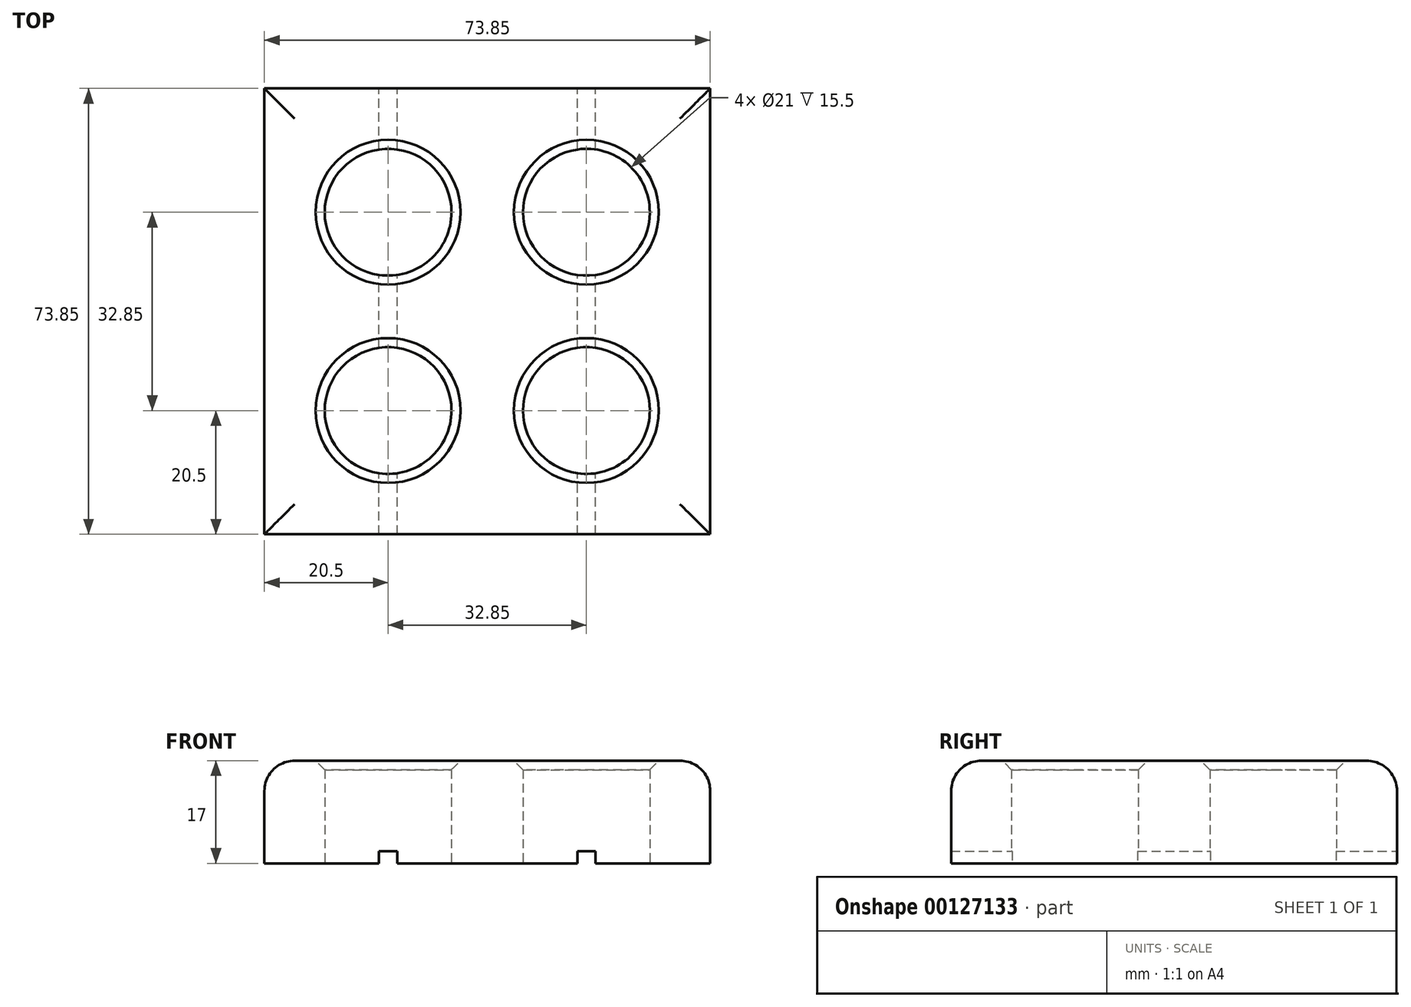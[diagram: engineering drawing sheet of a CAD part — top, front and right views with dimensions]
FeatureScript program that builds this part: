
annotation { "Feature Type Name" : "Feature", "Feature Type Description" : "" }
export const myFeature = defineFeature(function(context is Context, id is Id, definition is map)
    precondition{}
    {
        {
            var Q0;
            Q0=qCreatedBy(makeId("Top.planeOp"),FACE);
            var sketch = newSketch(context, id + "F0", { "sketchPlane" : qUnion([Q0])});
            skCircle(sketch, "E0", {"center": v(0, 0) * mm, "radius": 10.5 * mm});
            skCircle(sketch, "E1", {"center": v(0, -32.85) * mm, "radius": 10.5 * mm});
            skCircle(sketch, "E2", {"center": v(32.85, 0) * mm, "radius": 10.5 * mm});
            skCircle(sketch, "E3", {"center": v(32.85, -32.85) * mm, "radius": 10.5 * mm});
            skLineSegment(sketch, "E4.bottom", {"start": v(-20.5, 20.5) * mm, "end": v(53.35, 20.5) * mm});
            skLineSegment(sketch, "E4.top", {"start": v(-20.5, -53.35) * mm, "end": v(53.35, -53.35) * mm});
            skLineSegment(sketch, "E4.left", {"start": v(-20.5, 20.5) * mm, "end": v(-20.5, -53.35) * mm});
            skLineSegment(sketch, "E4.right", {"start": v(53.35, 20.5) * mm, "end": v(53.35, -53.35) * mm});
            skSolve(sketch);
        }
        {
            var Q0;
            Q0=makeQuery(id+"F0.imprint","IMPRINT",FACE,{"disambiguationData":[TD([[makeQuery(id+"F0.imprint","IMPRINT",EDGE,{"derivedFrom":sQuery(id+"F0.wireOp",EDGE,"E0")}),-1.0]])]});
            extrude(context, id + "F1", {"entities" : qUnion([Q0]), "depth" : 17 * mm});
        }
        {
            var Q0;
            Q0=makeQuery(id+"F1.opExtrude","CAP_EDGE",EDGE,{"disambiguationData":[OSD([sQuery(id+"F0.wireOp",EDGE,"E0")])],"isStart":false});
            var Q1;
            Q1=makeQuery(id+"F1.opExtrude","CAP_EDGE",EDGE,{"disambiguationData":[OSD([sQuery(id+"F0.wireOp",EDGE,"E2")])],"isStart":false});
            var Q2;
            Q2=makeQuery(id+"F1.opExtrude","CAP_EDGE",EDGE,{"disambiguationData":[OSD([sQuery(id+"F0.wireOp",EDGE,"E3")])],"isStart":false});
            var Q3;
            Q3=makeQuery(id+"F1.opExtrude","CAP_EDGE",EDGE,{"disambiguationData":[OSD([sQuery(id+"F0.wireOp",EDGE,"E1")])],"isStart":false});
            chamfer(context, id + "F2", {"entities" : qUnion([Q0, Q1, Q2, Q3]), "width" : 1.5 * mm, "tangentPropagation" : true});
        }
        {
            var Q0;
            Q0=makeQuery(id+"F1.opExtrude","CAP_EDGE",EDGE,{"disambiguationData":[OSD([sQuery(id+"F0.wireOp",EDGE,"E4.top")])],"isStart":false});
            var Q1;
            Q1=makeQuery(id+"F1.opExtrude","CAP_EDGE",EDGE,{"disambiguationData":[OSD([sQuery(id+"F0.wireOp",EDGE,"E4.left")])],"isStart":false});
            var Q2;
            Q2=makeQuery(id+"F1.opExtrude","CAP_EDGE",EDGE,{"disambiguationData":[OSD([sQuery(id+"F0.wireOp",EDGE,"E4.bottom")])],"isStart":false});
            var Q3;
            Q3=makeQuery(id+"F1.opExtrude","CAP_EDGE",EDGE,{"disambiguationData":[OSD([sQuery(id+"F0.wireOp",EDGE,"E4.right")])],"isStart":false});
            fillet(context, id + "F3", {"entities" : qUnion([Q0, Q1, Q2, Q3]), "radius" : 5 * mm, "tangentPropagation" : true, "allowEdgeOverflow" : false});
        }
        {
            var Q0;
            Q0=makeQuery(id+"F1.opExtrude","CAP_FACE",FACE,{"disambiguationData":[OSD([sQuery(id+"F0.wireOp",EDGE,"E0"),sQuery(id+"F0.wireOp",EDGE,"E1"),sQuery(id+"F0.wireOp",EDGE,"E2"),sQuery(id+"F0.wireOp",EDGE,"E3"),sQuery(id+"F0.wireOp",EDGE,"E4.bottom"),sQuery(id+"F0.wireOp",EDGE,"E4.top"),sQuery(id+"F0.wireOp",EDGE,"E4.left"),sQuery(id+"F0.wireOp",EDGE,"E4.right")])],"isStart":true});
            var sketch = newSketch(context, id + "F4", { "sketchPlane" : qUnion([Q0])});
            skLineSegment(sketch, "E5.bottom", {"start": v(-1.5, 53.35) * mm, "end": v(1.5, 53.35) * mm});
            skLineSegment(sketch, "E5.top", {"start": v(-1.5, -20.5) * mm, "end": v(1.5, -20.5) * mm});
            skLineSegment(sketch, "E5.left", {"start": v(-1.5, 53.35) * mm, "end": v(-1.5, -20.5) * mm});
            skLineSegment(sketch, "E5.right", {"start": v(1.5, 53.35) * mm, "end": v(1.5, -20.5) * mm});
            skLineSegment(sketch, "E6.bottom", {"start": v(31.35, 53.35) * mm, "end": v(34.35, 53.35) * mm});
            skLineSegment(sketch, "E6.top", {"start": v(31.35, -20.5) * mm, "end": v(34.35, -20.5) * mm});
            skLineSegment(sketch, "E6.left", {"start": v(31.35, 53.35) * mm, "end": v(31.35, -20.5) * mm});
            skLineSegment(sketch, "E6.right", {"start": v(34.35, 53.35) * mm, "end": v(34.35, -20.5) * mm});
            skSolve(sketch);
        }
        {
            var Q0;
            {var subQ0=sQuery(id+"F4.wireOp",EDGE,"E5.top");Q0=makeQuery(id+"F4.imprint","IMPRINT",FACE,{"disambiguationData":[TD([[makeQuery(id+"F4.imprint","IMPRINT",EDGE,{"derivedFrom":subQ0}),1.0]])]});}
            var Q1;
            {var subQ0=sQuery(id+"F4.wireOp",EDGE,"E5.left");var subQ1=makeQuery(id+"F1.opExtrude","CAP_EDGE",EDGE,{"disambiguationData":[OSD([sQuery(id+"F0.wireOp",EDGE,"E1")])],"isStart":true});var subQ2=makeQuery(id+"F4.imprint","INTERSECT",VERTEX,{"disambiguationData":[OD(0.0)],"derivedFrom":[subQ1,subQ0]});Q1=makeQuery(id+"F4.imprint","IMPRINT",FACE,{"disambiguationData":[TD([[makeQuery(id+"F4.imprint","IMPRINT",EDGE,{"disambiguationData":[TD([[subQ2,-1.0]])],"derivedFrom":subQ0}),1.0]])]});}
            var Q2;
            {var subQ0=sQuery(id+"F4.wireOp",EDGE,"E5.left");var subQ1=makeQuery(id+"F1.opExtrude","CAP_EDGE",EDGE,{"disambiguationData":[OSD([sQuery(id+"F0.wireOp",EDGE,"E1")])],"isStart":true});var subQ2=makeQuery(id+"F4.imprint","INTERSECT",VERTEX,{"disambiguationData":[OD(1.0)],"derivedFrom":[subQ1,subQ0]});Q2=makeQuery(id+"F4.imprint","IMPRINT",FACE,{"disambiguationData":[TD([[makeQuery(id+"F4.imprint","IMPRINT",EDGE,{"disambiguationData":[TD([[subQ2,-1.0]])],"derivedFrom":subQ0}),1.0]])]});}
            var Q3;
            {var subQ0=sQuery(id+"F4.wireOp",EDGE,"E5.left");var subQ1=makeQuery(id+"F1.opExtrude","CAP_EDGE",EDGE,{"disambiguationData":[OSD([sQuery(id+"F0.wireOp",EDGE,"E0")])],"isStart":true});var subQ2=makeQuery(id+"F4.imprint","INTERSECT",VERTEX,{"disambiguationData":[OD(0.0)],"derivedFrom":[subQ1,subQ0]});Q3=makeQuery(id+"F4.imprint","IMPRINT",FACE,{"disambiguationData":[TD([[makeQuery(id+"F4.imprint","IMPRINT",EDGE,{"disambiguationData":[TD([[subQ2,-1.0]])],"derivedFrom":subQ0}),1.0]])]});}
            var Q4;
            {var subQ0=sQuery(id+"F4.wireOp",EDGE,"E6.left");var subQ1=makeQuery(id+"F1.opExtrude","CAP_EDGE",EDGE,{"disambiguationData":[OSD([sQuery(id+"F0.wireOp",EDGE,"E3")])],"isStart":true});var subQ2=makeQuery(id+"F4.imprint","INTERSECT",VERTEX,{"disambiguationData":[OD(0.0)],"derivedFrom":[subQ1,subQ0]});Q4=makeQuery(id+"F4.imprint","IMPRINT",FACE,{"disambiguationData":[TD([[makeQuery(id+"F4.imprint","IMPRINT",EDGE,{"disambiguationData":[TD([[subQ2,-1.0]])],"derivedFrom":subQ0}),1.0]])]});}
            var Q5;
            {var subQ0=sQuery(id+"F4.wireOp",EDGE,"E6.left");var subQ1=makeQuery(id+"F1.opExtrude","CAP_EDGE",EDGE,{"disambiguationData":[OSD([sQuery(id+"F0.wireOp",EDGE,"E2")])],"isStart":true});var subQ2=makeQuery(id+"F4.imprint","INTERSECT",VERTEX,{"disambiguationData":[OD(0.0)],"derivedFrom":[subQ1,subQ0]});Q5=makeQuery(id+"F4.imprint","IMPRINT",FACE,{"disambiguationData":[TD([[makeQuery(id+"F4.imprint","IMPRINT",EDGE,{"disambiguationData":[TD([[subQ2,-1.0]])],"derivedFrom":subQ0}),1.0]])]});}
            var Q6;
            {var subQ0=sQuery(id+"F4.wireOp",EDGE,"E5.bottom");Q6=makeQuery(id+"F4.imprint","IMPRINT",FACE,{"disambiguationData":[TD([[makeQuery(id+"F4.imprint","IMPRINT",EDGE,{"derivedFrom":subQ0}),-1.0]])]});}
            var Q7;
            {var subQ0=sQuery(id+"F4.wireOp",EDGE,"E6.left");var subQ1=makeQuery(id+"F1.opExtrude","CAP_EDGE",EDGE,{"disambiguationData":[OSD([sQuery(id+"F0.wireOp",EDGE,"E3")])],"isStart":true});var subQ2=makeQuery(id+"F4.imprint","INTERSECT",VERTEX,{"disambiguationData":[OD(1.0)],"derivedFrom":[subQ1,subQ0]});Q7=makeQuery(id+"F4.imprint","IMPRINT",FACE,{"disambiguationData":[TD([[makeQuery(id+"F4.imprint","IMPRINT",EDGE,{"disambiguationData":[TD([[subQ2,-1.0]])],"derivedFrom":subQ0}),1.0]])]});}
            var Q8;
            {var subQ0=sQuery(id+"F4.wireOp",EDGE,"E6.top");Q8=makeQuery(id+"F4.imprint","IMPRINT",FACE,{"disambiguationData":[TD([[makeQuery(id+"F4.imprint","IMPRINT",EDGE,{"derivedFrom":subQ0}),1.0]])]});}
            var Q9;
            {var subQ0=sQuery(id+"F4.wireOp",EDGE,"E6.bottom");Q9=makeQuery(id+"F4.imprint","IMPRINT",FACE,{"disambiguationData":[TD([[makeQuery(id+"F4.imprint","IMPRINT",EDGE,{"derivedFrom":subQ0}),-1.0]])]});}
            extrude(context, id + "F5", {"entities" : qUnion([Q0, Q1, Q2, Q3, Q4, Q5, Q6, Q7, Q8, Q9]), "operationType" : NewBodyOperationType.REMOVE, "oppositeDirection" : true, "depth" : 2 * mm});
        }
    });
